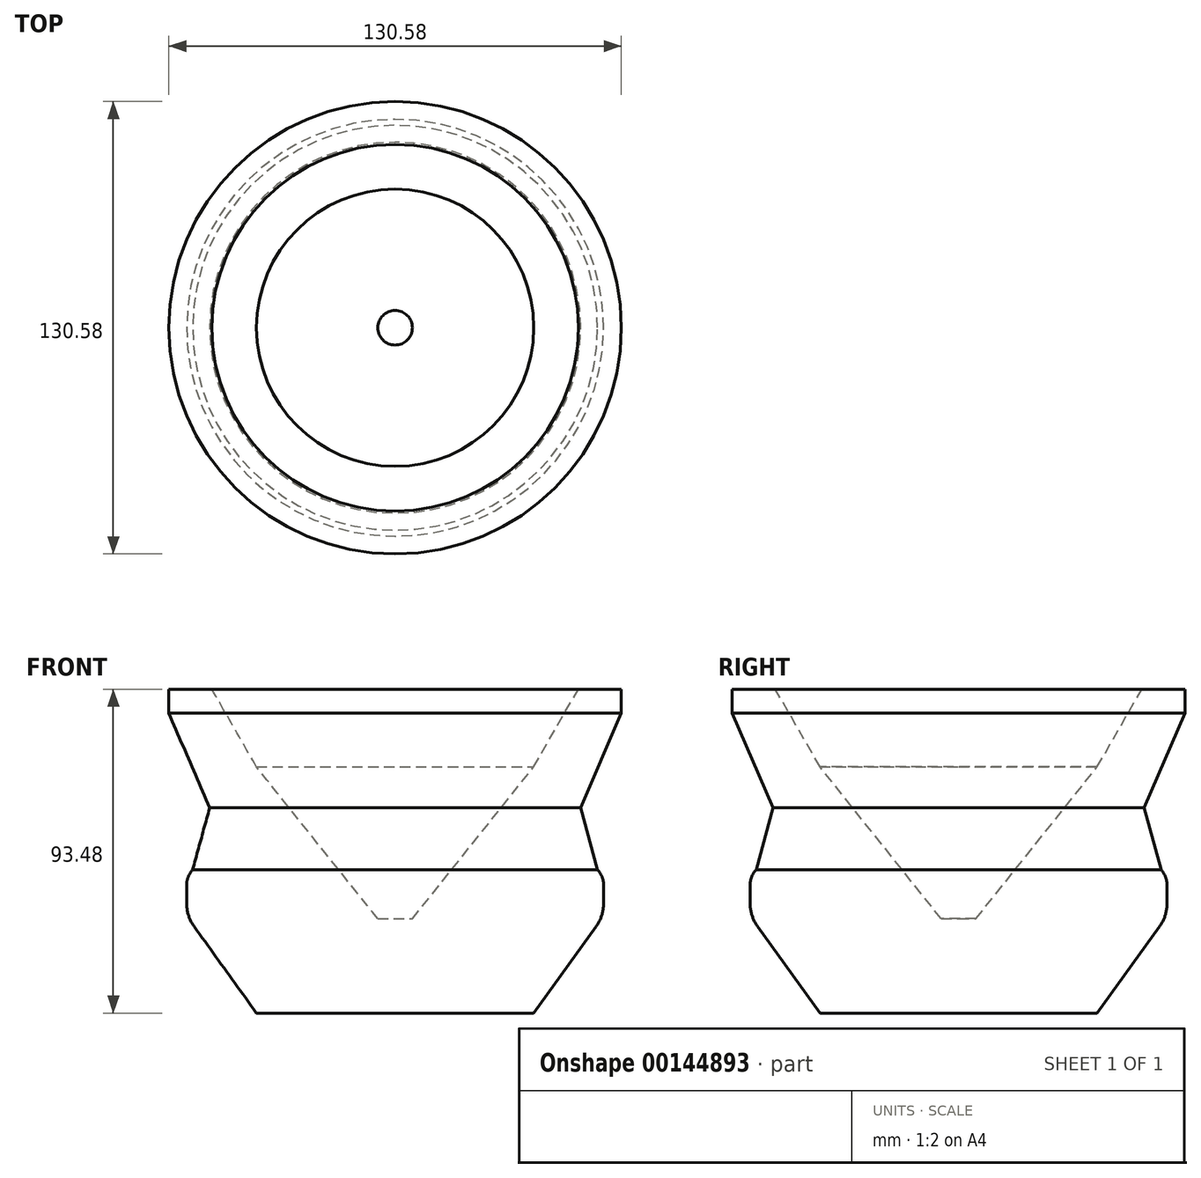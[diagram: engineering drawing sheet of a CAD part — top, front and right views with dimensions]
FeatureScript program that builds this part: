
annotation { "Feature Type Name" : "Feature", "Feature Type Description" : "" }
export const myFeature = defineFeature(function(context is Context, id is Id, definition is map)
    precondition{}
    {
        {
            var Q0;
            Q0=qCreatedBy(makeId("Front.planeOp"),FACE);
            var sketch = newSketch(context, id + "F0", { "sketchPlane" : qUnion([Q0])});
            skLineSegment(sketch, "E0", {"start": v(-5, 0) * mm, "end": v(35, 0) * mm});
            skLineSegment(sketch, "E1", {"start": v(35, 0) * mm, "end": v(35, 150) * mm, "construction": true});
            skLineSegment(sketch, "E2", {"start": v(35, 0) * mm, "end": v(52.98, 24.94) * mm});
            skLineSegment(sketch, "E3", {"start": v(55.16, 31.68) * mm, "end": v(55.16, 36.97) * mm});
            skLineSegment(sketch, "E4", {"start": v(-5, 0) * mm, "end": v(-5, 100.91) * mm, "construction": true});
            skLineSegment(sketch, "E5", {"start": v(35, 0) * mm, "end": v(-16.1, 0) * mm});
            skLineSegment(sketch, "E6", {"start": v(-5, 0) * mm, "end": v(-16.1, 0) * mm});
            skLineSegment(sketch, "E7", {"start": v(-5, 0) * mm, "end": v(-5, 90.63) * mm});
            skLineSegment(sketch, "E8", {"start": v(35, 71.06) * mm, "end": v(0, 27.2) * mm});
            skLineSegment(sketch, "E9", {"start": v(0, 27.2) * mm, "end": v(-5, 27.2) * mm});
            skPoint(sketch, "E10.endSnap0", {"position": v(-5, 45.31) * mm});
            skPoint(sketch, "E11.visualSharp", {"position": v(35, 75.64) * mm});
            skPoint(sketch, "E12.visualSharp", {"position": v(55.16, 39.93) * mm});
            skArc(sketch, "E12.filletArc", {"start": v(55.16, 36.97) * mm, "mid": v(54.7, 39.32) * mm, "end": v(53.42, 41.33) * mm});
            skPoint(sketch, "E13.visualSharp", {"position": v(55.16, 27.96) * mm});
            skArc(sketch, "E13.filletArc", {"start": v(52.98, 24.94) * mm, "mid": v(54.6, 28.14) * mm, "end": v(55.16, 31.68) * mm});
            skPoint(sketch, "E14.visualSharp", {"position": v(108.57, 93.48) * mm});
            skLineSegment(sketch, "E15", {"start": v(53.42, 41.33) * mm, "end": v(48.53, 59.2) * mm});
            skPoint(sketch, "E16.visualSharp", {"position": v(46.88, 65.26) * mm});
            skLineSegment(sketch, "E17", {"start": v(47.88, 93.48) * mm, "end": v(35, 71.06) * mm});
            skLineSegment(sketch, "E18", {"start": v(48.53, 59.2) * mm, "end": v(60.3, 86.58) * mm});
            skLineSegment(sketch, "E19", {"start": v(60.3, 86.58) * mm, "end": v(60.3, 93.4) * mm});
            skLineSegment(sketch, "E20", {"start": v(60.3, 93.4) * mm, "end": v(47.88, 93.48) * mm});
            skSolve(sketch);
        }
        {
            var Q0;
            Q0=makeQuery(id+"F0.imprint","IMPRINT",FACE,{"disambiguationData":[TD([[makeQuery(id+"F0.imprint","IMPRINT",EDGE,{"derivedFrom":sQuery(id+"F0.wireOp",EDGE,"E2")}),1.0]])]});
            var Q1;
            Q1=sQuery(id+"F0.wireOp",EDGE,"E4");
            revolve(context, id + "F1", {"entities" : qUnion([Q0]), "axis" : qUnion([Q1]), "revolveType" : RevolveType.FULL});
        }
    });
